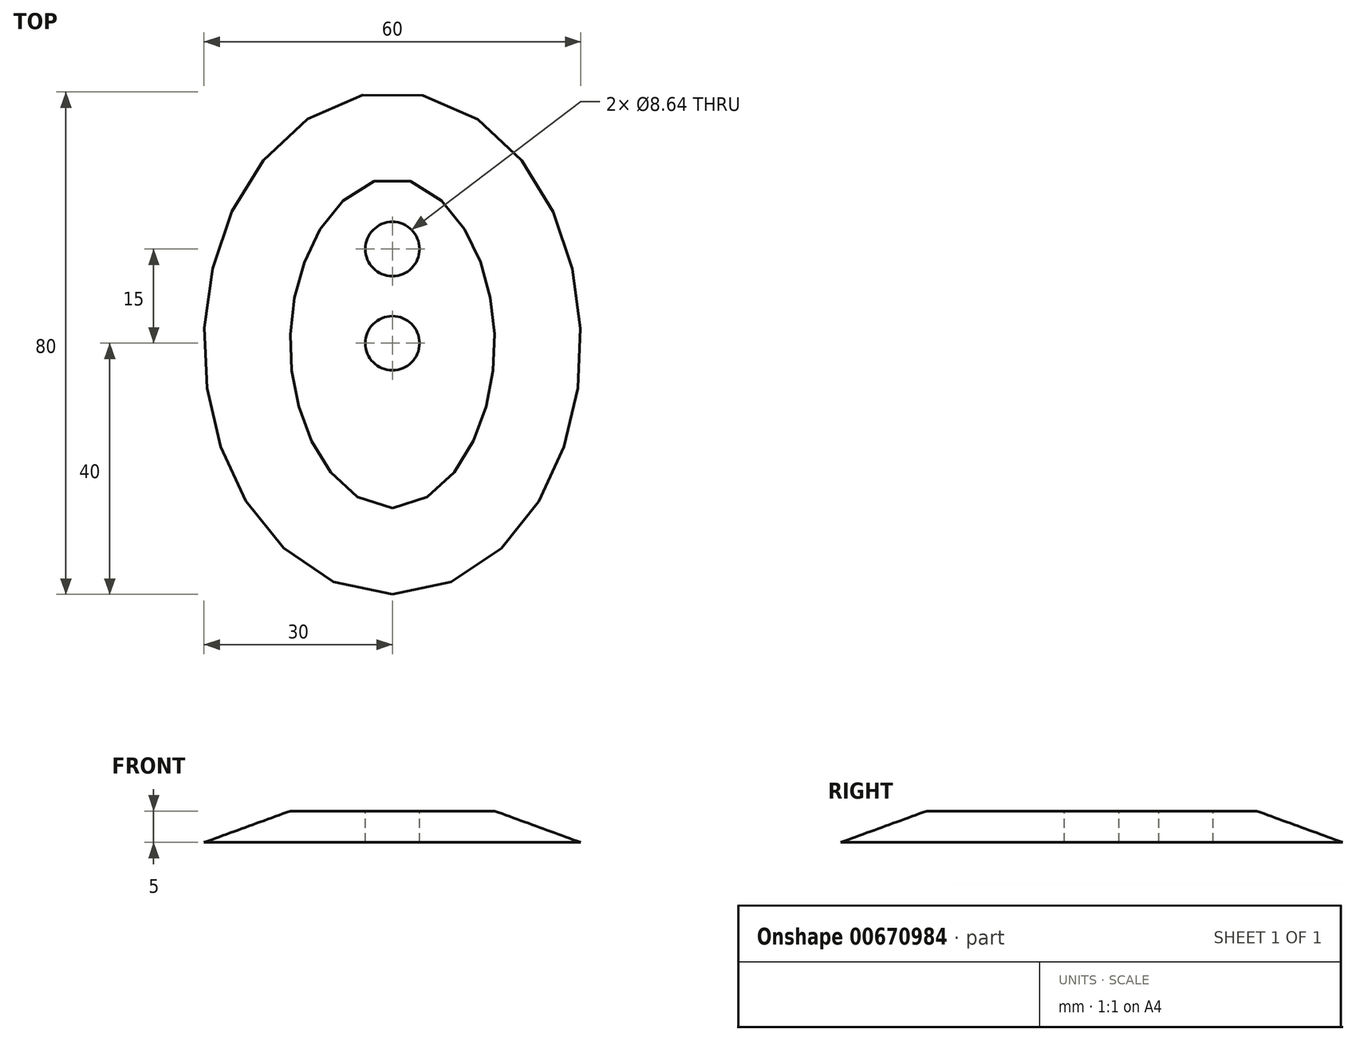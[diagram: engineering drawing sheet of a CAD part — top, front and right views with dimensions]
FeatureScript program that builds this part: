
annotation { "Feature Type Name" : "Feature", "Feature Type Description" : "" }
export const myFeature = defineFeature(function(context is Context, id is Id, definition is map)
    precondition{}
    {
        {
            var Q0;
            Q0=qCreatedBy(makeId("Top.planeOp"),FACE);
            var sketch = newSketch(context, id + "F0", { "sketchPlane" : qUnion([Q0])});
            skEllipse(sketch, "E0", {"center": v(0, 0) * mm, "majorRadius": 40 * mm, "minorRadius": 30 * mm, "majorAxis": v(0, 1)});
            skCircle(sketch, "E1", {"center": v(0, 0) * mm, "radius": 4.32 * mm});
            skSolve(sketch);
        }
        {
            var Q0;
            Q0 = qSketchRegion(id + "F0", true);
            var Q1;
            Q1=makeQuery(id+"F0.imprint","IMPRINT",FACE,{"disambiguationData":[TD([[makeQuery(id+"F0.imprint","IMPRINT",EDGE,{"derivedFrom":sQuery(id+"F0.wireOp",EDGE,"E1")}),1.0]])]});
            extrude(context, id + "F1", {"entities" : qUnion([Q0, Q1]), "depth" : 5 * mm, "offsetDistance" : 25 * mm, "hasDraft" : true, "draftAngle" : 70 * degree, "draftPullDirection" : true});
        }
        {
            var Q0;
            Q0=makeQuery(id+"F1.opExtrude","CAP_FACE",FACE,{"disambiguationData":[OSD([sQuery(id+"F0.wireOp",EDGE,"E0")])],"isStart":false});
            var sketch = newSketch(context, id + "F2", { "sketchPlane" : qUnion([Q0])});
            skCircle(sketch, "E2", {"center": v(0, 0) * mm, "radius": 4.32 * mm});
            skCircle(sketch, "E3", {"center": v(0, 15) * mm, "radius": 4.32 * mm});
            skSolve(sketch);
        }
        {
            var Q0;
            Q0 = qSketchRegion(id + "F2", true);
            extrude(context, id + "F3", {"entities" : qUnion([Q0]), "operationType" : NewBodyOperationType.REMOVE, "endBound" : BoundingType.UP_TO_NEXT, "oppositeDirection" : true, "depth" : 25 * mm, "offsetDistance" : 25 * mm});
        }
    });
